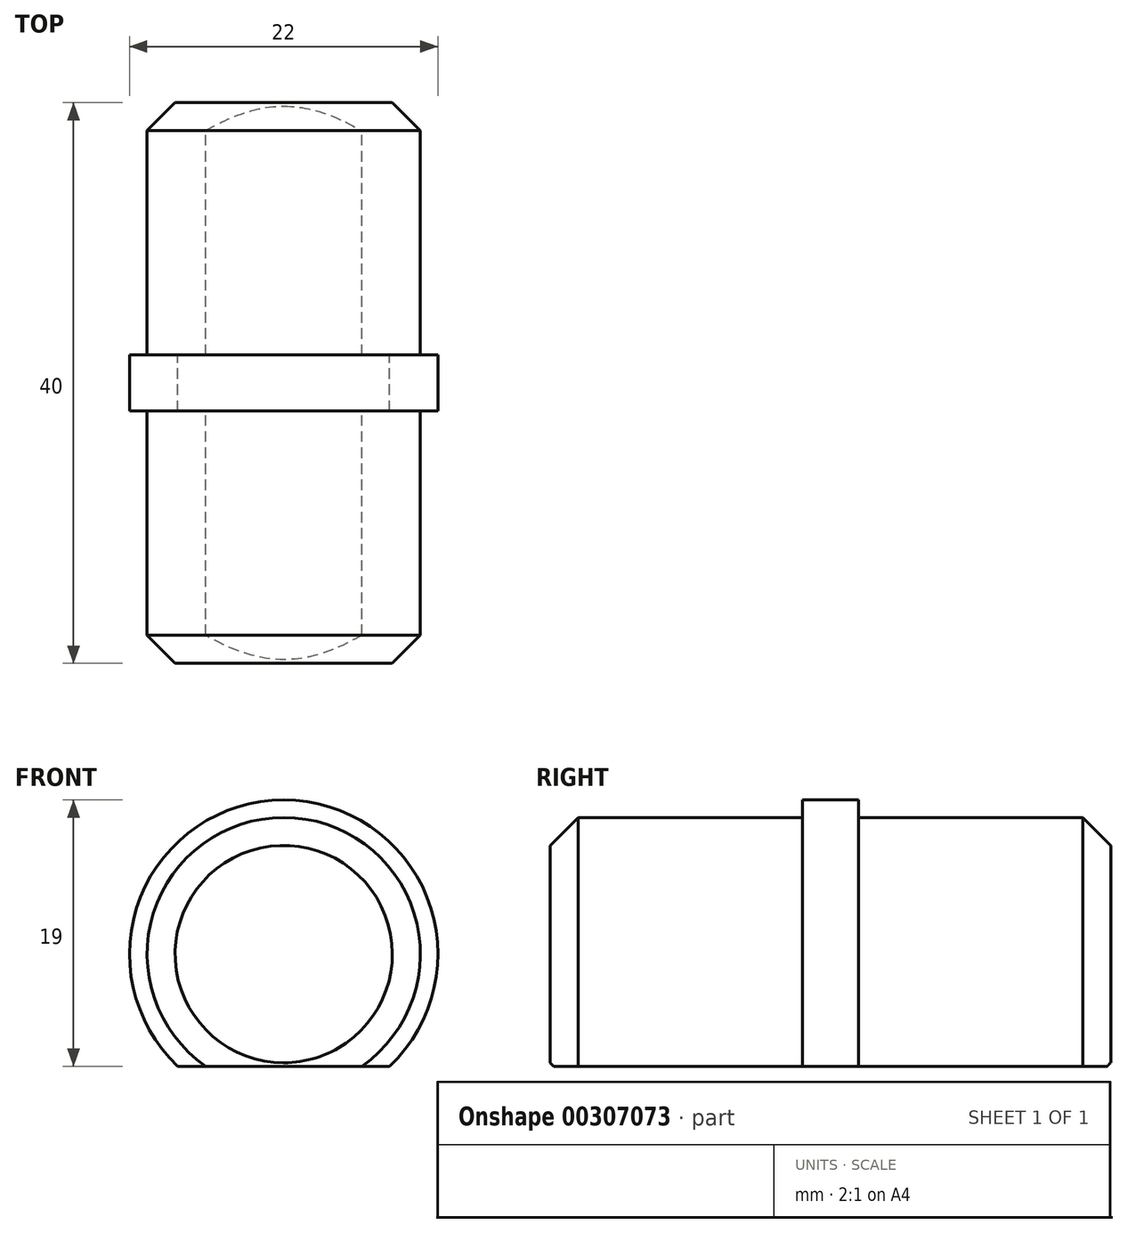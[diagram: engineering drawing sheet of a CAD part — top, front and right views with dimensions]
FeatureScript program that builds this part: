
annotation { "Feature Type Name" : "Feature", "Feature Type Description" : "" }
export const myFeature = defineFeature(function(context is Context, id is Id, definition is map)
    precondition{}
    {
        {
            var Q0;
            Q0=qCreatedBy(makeId("Front.planeOp"),FACE);
            var sketch = newSketch(context, id + "F0", { "sketchPlane" : qUnion([Q0])});
            skCircle(sketch, "E0", {"center": v(0, 0) * mm, "radius": 9.75 * mm});
            skSolve(sketch);
        }
        {
            var Q0;
            Q0 = qSketchRegion(id + "F0", true);
            extrude(context, id + "F1", {"entities" : qUnion([Q0]), "depth" : 20 * mm, "hasSecondDirection" : true, "secondDirectionOppositeDirection" : true, "secondDirectionDepth" : 20 * mm});
        }
        {
            var Q0;
            Q0=qCreatedBy(makeId("Front.planeOp"),FACE);
            var sketch = newSketch(context, id + "F2", { "sketchPlane" : qUnion([Q0])});
            skCircle(sketch, "E1", {"center": v(0, 0) * mm, "radius": 11 * mm});
            skSolve(sketch);
        }
        {
            var Q0;
            Q0 = qSketchRegion(id + "F2", true);
            extrude(context, id + "F3", {"entities" : qUnion([Q0]), "operationType" : NewBodyOperationType.ADD, "depth" : 2 * mm, "hasSecondDirection" : true, "secondDirectionOppositeDirection" : true, "secondDirectionDepth" : 2 * mm});
        }
        {
            var Q0;
            Q0=qCreatedBy(makeId("Front.planeOp"),FACE);
            var sketch = newSketch(context, id + "F4", { "sketchPlane" : qUnion([Q0])});
            skLineSegment(sketch, "E2.bottom", {"start": v(-32.83, -48.58) * mm, "end": v(39.07, -48.58) * mm});
            skLineSegment(sketch, "E2.top", {"start": v(-32.83, -8) * mm, "end": v(39.07, -8) * mm});
            skLineSegment(sketch, "E2.left", {"start": v(-32.83, -48.58) * mm, "end": v(-32.83, -8) * mm});
            skLineSegment(sketch, "E2.right", {"start": v(39.07, -48.58) * mm, "end": v(39.07, -8) * mm});
            skSolve(sketch);
        }
        {
            var Q0;
            Q0 = qSketchRegion(id + "F4", true);
            extrude(context, id + "F5", {"entities" : qUnion([Q0]), "operationType" : NewBodyOperationType.REMOVE, "oppositeDirection" : true, "depth" : 25 * mm, "hasSecondDirection" : true, "secondDirectionOppositeDirection" : false, "secondDirectionDepth" : 25 * mm});
        }
        {
            var Q0;
            Q0=makeQuery(id+"F1.opExtrude","CAP_EDGE",EDGE,{"disambiguationData":[OSD([sQuery(id+"F0.wireOp",EDGE,"E0")])],"isStart":false});
            var Q1;
            Q1=makeQuery(id+"F1.opExtrude","CAP_EDGE",EDGE,{"disambiguationData":[OSD([sQuery(id+"F0.wireOp",EDGE,"E0")])],"isStart":true});
            chamfer(context, id + "F6", {"entities" : qUnion([Q0, Q1]), "width" : 2 * mm, "tangentPropagation" : true});
        }
    });
